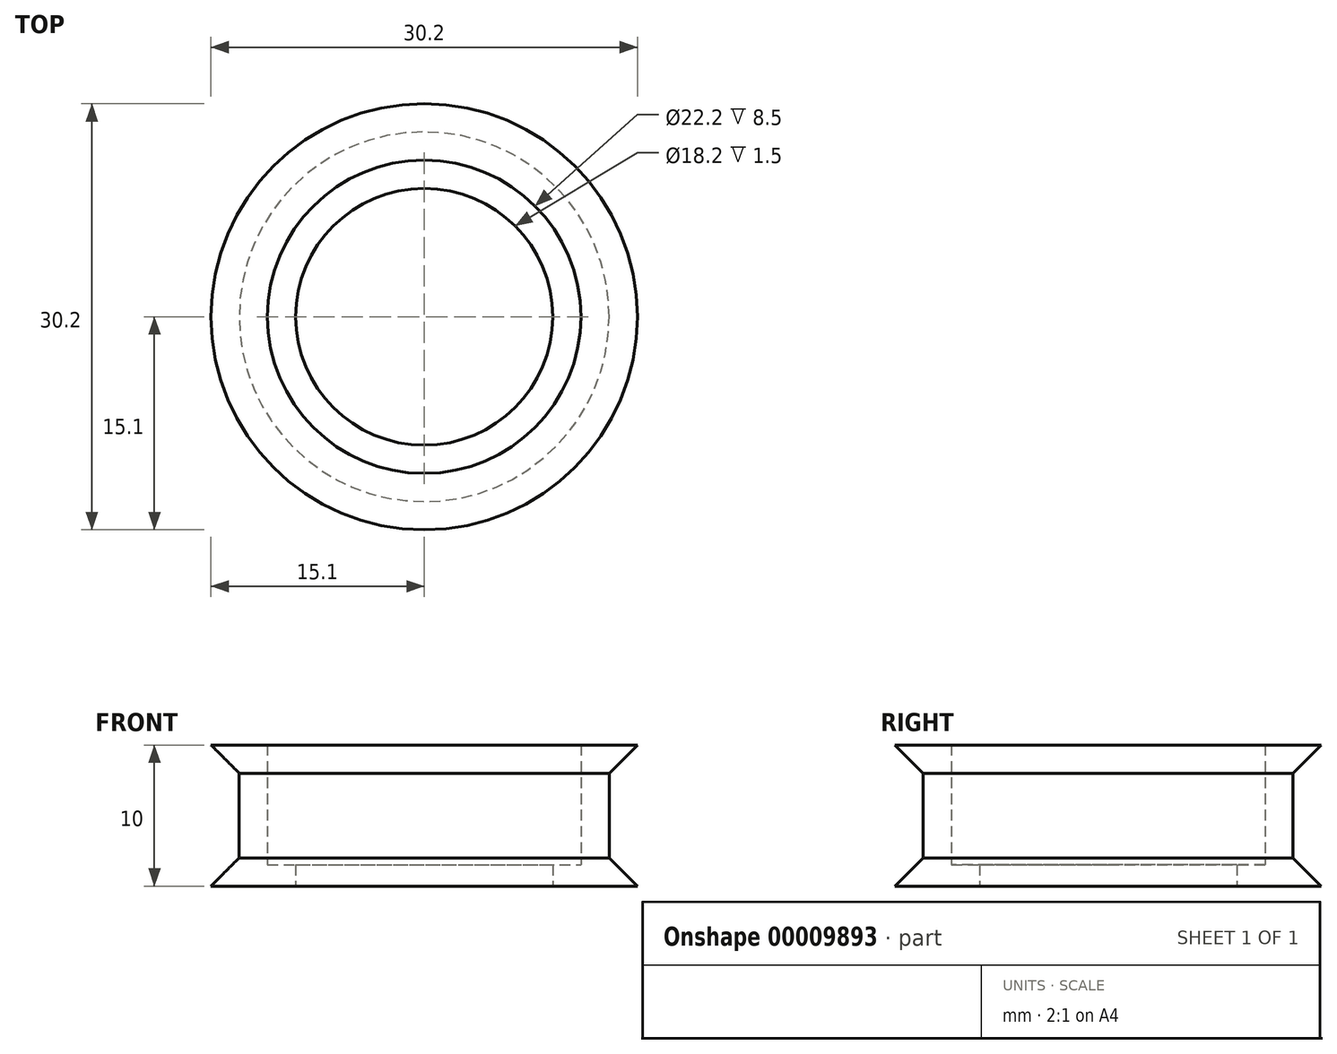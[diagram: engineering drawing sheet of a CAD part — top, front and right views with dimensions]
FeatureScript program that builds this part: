
annotation { "Feature Type Name" : "Feature", "Feature Type Description" : "" }
export const myFeature = defineFeature(function(context is Context, id is Id, definition is map)
    precondition{}
    {
        {
            var Q0;
            Q0=qCreatedBy(makeId("Front.planeOp"),FACE);
            var sketch = newSketch(context, id + "F0", { "sketchPlane" : qUnion([Q0])});
            skLineSegment(sketch, "E0", {"start": v(11.1, 4.8) * mm, "end": v(15.1, 4.8) * mm});
            skLineSegment(sketch, "E1", {"start": v(15.1, 4.8) * mm, "end": v(13.1, 2.8) * mm});
            skLineSegment(sketch, "E2", {"start": v(13.1, 2.8) * mm, "end": v(13.1, -3.2) * mm});
            skLineSegment(sketch, "E3", {"start": v(13.1, -3.2) * mm, "end": v(15.1, -5.2) * mm});
            skLineSegment(sketch, "E4", {"start": v(15.1, -5.2) * mm, "end": v(11.1, -5.2) * mm});
            skLineSegment(sketch, "E5", {"start": v(11.1, -5.2) * mm, "end": v(11.1, 4.8) * mm});
            skLineSegment(sketch, "E6", {"start": v(0, -3.77) * mm, "end": v(0, 4.95) * mm, "construction": true});
            skLineSegment(sketch, "E7.bottom", {"start": v(11.1, -5.2) * mm, "end": v(9.1, -5.2) * mm});
            skLineSegment(sketch, "E7.top", {"start": v(11.1, -3.7) * mm, "end": v(9.1, -3.7) * mm});
            skLineSegment(sketch, "E7.left", {"start": v(11.1, -5.2) * mm, "end": v(11.1, -3.7) * mm});
            skLineSegment(sketch, "E7.right", {"start": v(9.1, -5.2) * mm, "end": v(9.1, -3.7) * mm});
            skSolve(sketch);
        }
        {
            var Q0;
            Q0 = qSketchRegion(id + "F0", true);
            var Q1;
            Q1=sQuery(id+"F0.wireOp",EDGE,"E6");
            revolve(context, id + "F1", {"entities" : qUnion([Q0]), "axis" : qUnion([Q1]), "revolveType" : RevolveType.FULL});
        }
    });
